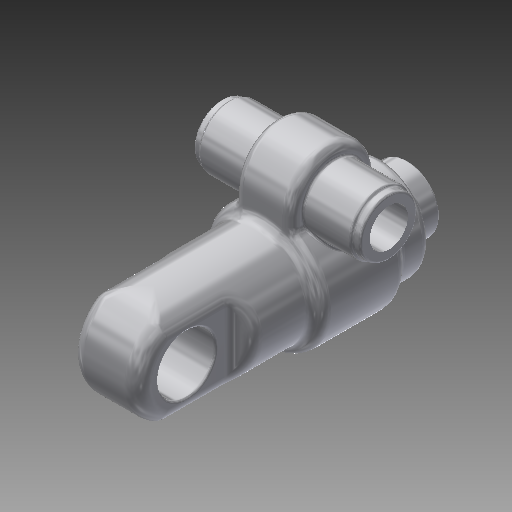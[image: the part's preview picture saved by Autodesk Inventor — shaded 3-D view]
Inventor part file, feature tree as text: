
AUTODESK INVENTOR PART (.ipt)
format: ipt  version: 2019 (Build 230136000, 136)  size: 605,696 bytes
history: native  units: mm
features: fillet x12, sketch x11, extrude x10, projected_geometry x7, plane x2, revolve x1
ambient origin geometry x8: Origin, YZ Plane, XZ Plane, XY Plane, X Axis, Y Axis, Z Axis, Center Point
bodies: Solid1 (feature_tree)
feature tree (43):
  plane  "Work Plane1"
  extrude  "Extrusion1"  Depth=58.28mm TaperAngle=0.0deg
  extrude  "Extrusion2"  Depth=58.28mm TaperAngle=0.0deg
  extrude  "Extrusion3"  Depth=7.217mm
  extrude  "Extrusion4"  Depth=10.229mm
  fillet  "Fillet1"  Radius=20.38mm
  fillet  "Fillet2"  Radius=2.44mm
  fillet  "Fillet3"  Radius=2.17mm
  fillet  "Fillet4"  Radius=3.0mm
  plane  "Work Plane2"
  extrude  "Extrusion5"  [1 undecoded]
  fillet  "Fillet5"  Radius=15.87mm
  fillet  "Fillet6"  Radius=25.0mm
  fillet  "Fillet7"  Radius=12.0mm
  extrude  "Extrusion6"  Depth=18.02mm TaperAngle=0.0deg
  extrude  "Extrusion7"  Depth=2.0mm
  fillet  "Fillet8"  Radius=2.0mm
  extrude  "Extrusion8"  Depth=32.0mm TaperAngle=0.0deg
  extrude  "Extrusion9"  Depth=0.5mm TaperAngle=0.0deg
  fillet  "Fillet9"  Radius=0.5mm
  fillet  "Fillet10"  Radius=8.0mm
  revolve  "Revolution1"  [1 undecoded]
  extrude  "Extrusion10"  Depth=0.5mm
  fillet  "Fillet11"  Radius=0.5mm
  fillet  "Fillet12"  Radius=8.5mm
  sketch  "Sketch2"  dims[d2=21.0mm d3=58.28mm d4=0.0mm]
  sketch  "Sketch3"  dims[d5=12.0mm d6=58.28mm d7=0.0mm]
  sketch  "Sketch4"  dims[d8=7.217mm d9=7.217mm]
  sketch  "Sketch5"  dims[d10=20.38mm d11=0.0mm d12=10.229mm d13=20.38mm d14=0.0mm d15=2.44mm d16=2.17mm d17=3.0mm]
  sketch  "Sketch6"  dims[d18=0.5mm d19=-23.0mm d20=15.87mm d21=25.0mm d22=12.0mm]
  sketch  "Sketch7"  dims[d24=12.0mm d25=18.02mm d26=0.0mm]
  projected_geometry  "Projected Loop2"
  sketch  "Sketch8"  dims[d27=9.01mm d28=2.0mm d29=2.0mm]
  projected_geometry  "Projected Loop3"
  sketch  "Sketch9"  dims[d30=13.0mm d31=32.0mm d32=0.0mm]
  projected_geometry  "Projected Loop4"
  sketch  "Sketch10"  dims[d33=12.0mm d34=35.0mm d35=0.0mm d36=0.5mm d37=8.0mm]
  sketch  "Sketch11"  dims[d38=43.0mm d39=0.0mm d40=13.5mm]
  projected_geometry  "Projected Loop5"
  projected_geometry  "Projected Loop6"
  sketch  "Sketch12"  dims[d41=5.5mm d42=0.0mm d43=2.0mm d44=0.5mm d45=8.5mm d46=12.0mm d47=7.5mm d48=32.0mm d49=12.5mm d50=20.25mm d51=90.0deg d52=10.0mm d53=0.0mm d54=1.0mm d55=0.5mm]
  projected_geometry  "Projected Loop7"
  projected_geometry  "Projected Loop8"
note: 2 required parameter values undecoded (feature->parameter linkage not recoverable at this tier; creation-order binding heuristic only, values carry confidence <= 0.55)